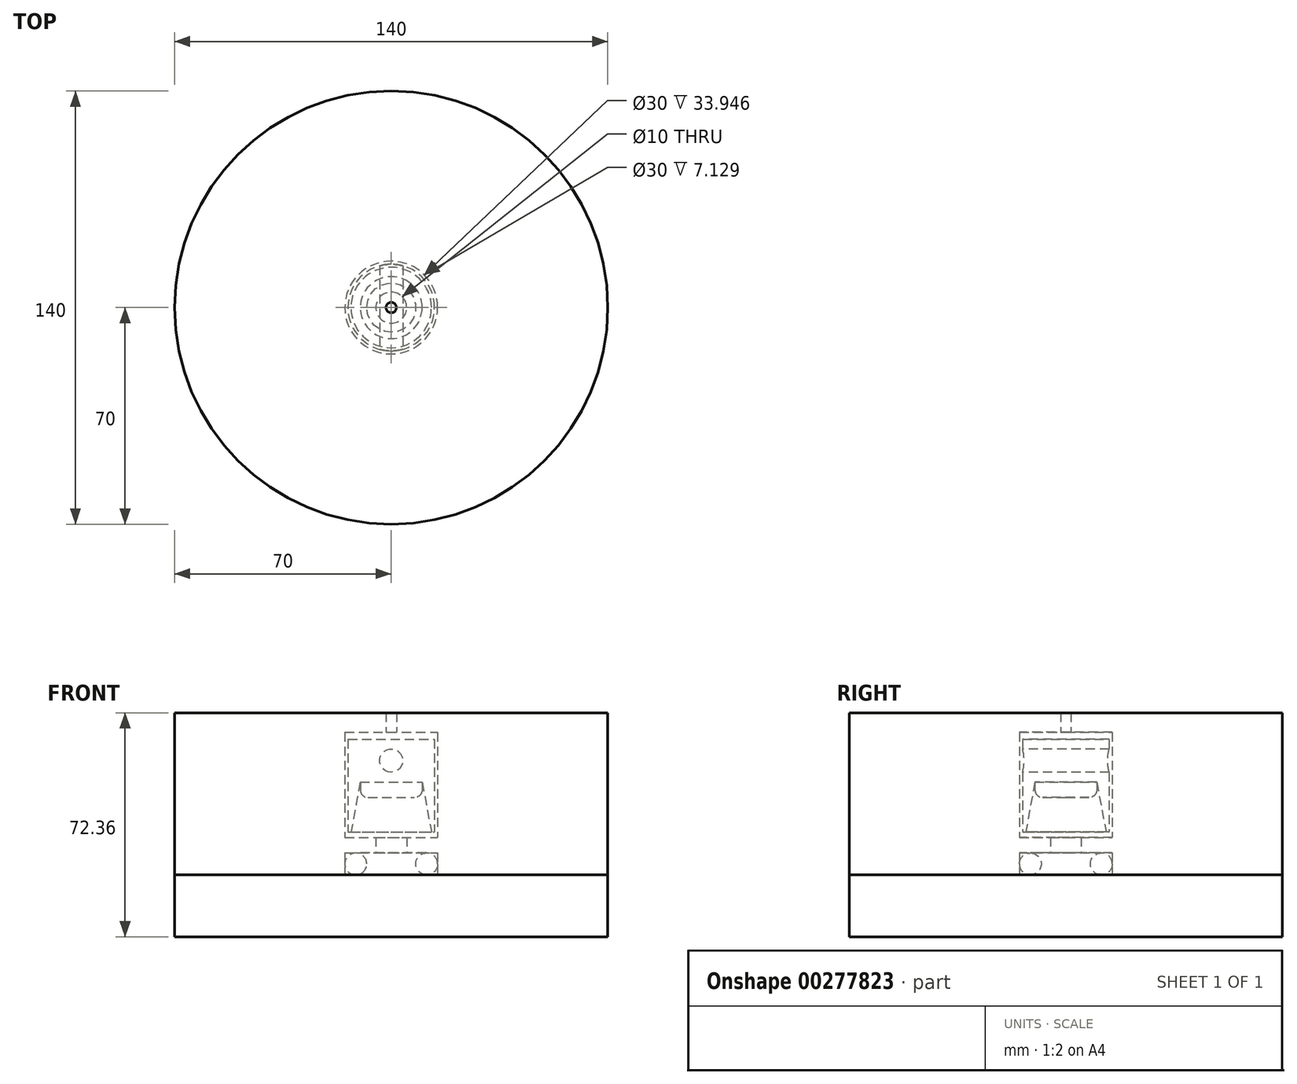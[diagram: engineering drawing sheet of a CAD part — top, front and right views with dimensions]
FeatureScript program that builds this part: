
annotation { "Feature Type Name" : "Feature", "Feature Type Description" : "" }
export const myFeature = defineFeature(function(context is Context, id is Id, definition is map)
    precondition{}
    {
        {
            var Q0;
            Q0=qCreatedBy(makeId("Front.planeOp"),FACE);
            var sketch = newSketch(context, id + "F0", { "sketchPlane" : qUnion([Q0])});
            skLineSegment(sketch, "E0", {"start": v(0, 0) * mm, "end": v(0, 80) * mm, "construction": true});
            skLineSegment(sketch, "E1.bottom", {"start": v(0, 0) * mm, "end": v(15, 0) * mm, "construction": true});
            skLineSegment(sketch, "E1.top", {"start": v(0, 30) * mm, "end": v(15, 30) * mm, "construction": true});
            skLineSegment(sketch, "E1.left", {"start": v(0, 0) * mm, "end": v(0, 30) * mm, "construction": true});
            skLineSegment(sketch, "E1.right", {"start": v(15, 0) * mm, "end": v(15, 30) * mm, "construction": true});
            skLineSegment(sketch, "E2", {"start": v(15, 0) * mm, "end": v(11.46, 3.54) * mm, "construction": true});
            skCircle(sketch, "E3", {"center": v(11.46, 3.54) * mm, "radius": 3.54 * mm});
            skLineSegment(sketch, "E4.bottom", {"start": v(0, 30) * mm, "end": v(10, 30) * mm});
            skLineSegment(sketch, "E4.top", {"start": v(0, 25) * mm, "end": v(7.5, 25) * mm});
            skLineSegment(sketch, "E4.left", {"start": v(0, 30) * mm, "end": v(0, 25) * mm});
            skLineSegment(sketch, "E4.right", {"start": v(10, 30) * mm, "end": v(10, 27.5) * mm});
            skPoint(sketch, "E5.visualSharp", {"position": v(10, 25) * mm});
            skArc(sketch, "E5.filletArc", {"start": v(7.5, 25) * mm, "mid": v(9.27, 25.73) * mm, "end": v(10, 27.5) * mm});
            skLineSegment(sketch, "E6.bottom", {"start": v(0, 30) * mm, "end": v(14, 30) * mm, "construction": true});
            skLineSegment(sketch, "E6.top", {"start": v(0, 13.8) * mm, "end": v(14, 13.8) * mm, "construction": true});
            skLineSegment(sketch, "E6.left", {"start": v(0, 30) * mm, "end": v(0, 13.8) * mm, "construction": true});
            skLineSegment(sketch, "E6.right", {"start": v(14, 30) * mm, "end": v(14, 13.8) * mm, "construction": true});
            skLineSegment(sketch, "E7.bottom", {"start": v(15, 7.13) * mm, "end": v(5, 7.13) * mm});
            skLineSegment(sketch, "E7.top", {"start": v(15, 12.13) * mm, "end": v(5, 12.13) * mm});
            skLineSegment(sketch, "E7.left", {"start": v(15, 7.13) * mm, "end": v(15, 12.13) * mm});
            skLineSegment(sketch, "E7.right", {"start": v(5, 7.13) * mm, "end": v(5, 12.13) * mm});
            skLineSegment(sketch, "E8", {"start": v(10, 30) * mm, "end": v(13, 13.8) * mm});
            skLineSegment(sketch, "E9", {"start": v(13, 13.8) * mm, "end": v(14, 13.8) * mm});
            skLineSegment(sketch, "E10", {"start": v(14, 13.8) * mm, "end": v(14, 43.84) * mm});
            skLineSegment(sketch, "E11", {"start": v(14, 43.84) * mm, "end": v(0, 43.84) * mm});
            skLineSegment(sketch, "E12", {"start": v(0, 43.84) * mm, "end": v(0, 30) * mm});
            skCircle(sketch, "E13", {"center": v(0, 36.92) * mm, "radius": 3.75 * mm});
            skLineSegment(sketch, "E14.bottom", {"start": v(0, 0) * mm, "end": v(70, 0) * mm});
            skLineSegment(sketch, "E14.top", {"start": v(0, -20) * mm, "end": v(70, -20) * mm});
            skLineSegment(sketch, "E14.left", {"start": v(0, 0) * mm, "end": v(0, -20) * mm});
            skLineSegment(sketch, "E14.right", {"start": v(70, 0) * mm, "end": v(70, -20) * mm});
            skLineSegment(sketch, "E15", {"start": v(15, 12.13) * mm, "end": v(15, 46.08) * mm});
            skLineSegment(sketch, "E16", {"start": v(15, 46.08) * mm, "end": v(1.68, 46.08) * mm});
            skLineSegment(sketch, "E17", {"start": v(1.68, 46.08) * mm, "end": v(1.68, 52.36) * mm});
            skLineSegment(sketch, "E18", {"start": v(1.68, 52.36) * mm, "end": v(70, 52.36) * mm});
            skLineSegment(sketch, "E19", {"start": v(70, 52.36) * mm, "end": v(70, 0) * mm});
            skLineSegment(sketch, "E20", {"start": v(70, 0) * mm, "end": v(15, 0) * mm});
            skLineSegment(sketch, "E21", {"start": v(15, 0) * mm, "end": v(15, 7.13) * mm});
            skSolve(sketch);
        }
        {
            var Q0;
            {var subQ0=sQuery(id+"F0.wireOp",EDGE,"E13");var subQ1=sQuery(id+"F0.wireOp",EDGE,"E12");var subQ2=makeQuery(id+"F0.imprint","INTERSECT",VERTEX,{"disambiguationData":[OD(0.0)],"derivedFrom":[subQ1,subQ0]});Q0=makeQuery(id+"F0.imprint","IMPRINT",FACE,{"disambiguationData":[TD([[makeQuery(id+"F0.imprint","IMPRINT",EDGE,{"disambiguationData":[TD([[subQ2,-1.0]])],"derivedFrom":subQ1}),1.0]])]});}
            var Q1;
            {var subQ1=sQuery(id+"F0.wireOp",EDGE,"E4.bottom");Q1=makeQuery(id+"F0.imprint","IMPRINT",FACE,{"disambiguationData":[TD([[makeQuery(id+"F0.imprint","IMPRINT",EDGE,{"derivedFrom":subQ1}),1.0]])]});}
            var Q2;
            Q2=sQuery(id+"F0.wireOp",EDGE,"E1.left");
            revolve(context, id + "F1", {"entities" : qUnion([Q0, Q1]), "axis" : qUnion([Q2]), "revolveType" : RevolveType.FULL});
        }
        {
            var Q0;
            {var subQ0=sQuery(id+"F0.wireOp",EDGE,"E13");var subQ1=sQuery(id+"F0.wireOp",EDGE,"E12");var subQ2=makeQuery(id+"F0.imprint","INTERSECT",VERTEX,{"disambiguationData":[OD(0.0)],"derivedFrom":[subQ1,subQ0]});Q0=makeQuery(id+"F0.imprint","IMPRINT",FACE,{"disambiguationData":[TD([[makeQuery(id+"F0.imprint","IMPRINT",EDGE,{"disambiguationData":[TD([[subQ2,-1.0]])],"derivedFrom":subQ1}),-1.0]])]});}
            var Q1;
            {var subQ0=sQuery(id+"F0.wireOp",EDGE,"E13");var subQ1=sQuery(id+"F0.wireOp",EDGE,"E12");var subQ2=makeQuery(id+"F0.imprint","INTERSECT",VERTEX,{"disambiguationData":[OD(0.0)],"derivedFrom":[subQ1,subQ0]});Q1=makeQuery(id+"F0.imprint","IMPRINT",FACE,{"disambiguationData":[TD([[makeQuery(id+"F0.imprint","IMPRINT",EDGE,{"disambiguationData":[TD([[subQ2,-1.0]])],"derivedFrom":subQ1}),1.0]])]});}
            var Q2;
            Q2=sQuery(id+"F0.wireOp",EDGE,"E13");
            extrude(context, id + "F2", {"entities" : qUnion([Q0, Q1]), "operationType" : NewBodyOperationType.REMOVE, "surfaceEntities" : qUnion([Q2]), "oppositeDirection" : true, "depth" : 28 * mm, "symmetric" : true});
        }
        {
            var Q0;
            Q0=makeQuery(id+"F0.imprint","IMPRINT",FACE,{"disambiguationData":[TD([[makeQuery(id+"F0.imprint","IMPRINT",EDGE,{"derivedFrom":sQuery(id+"F0.wireOp",EDGE,"E3")}),1.0]])]});
            var Q1;
            Q1=sQuery(id+"F0.wireOp",EDGE,"E1.left");
            revolve(context, id + "F3", {"entities" : qUnion([Q0]), "axis" : qUnion([Q1]), "revolveType" : RevolveType.FULL});
        }
        {
            var Q0;
            Q0=makeQuery(id+"F0.imprint","IMPRINT",FACE,{"disambiguationData":[TD([[makeQuery(id+"F0.imprint","IMPRINT",EDGE,{"derivedFrom":sQuery(id+"F0.wireOp",EDGE,"E4.bottom")}),-1.0]])]});
            var Q1;
            Q1=sQuery(id+"F0.wireOp",EDGE,"E1.left");
            revolve(context, id + "F4", {"entities" : qUnion([Q0]), "axis" : qUnion([Q1]), "revolveType" : RevolveType.FULL});
        }
        {
            var Q0;
            {var subQ0=sQuery(id+"F0.wireOp",EDGE,"E7.left");Q0=makeQuery(id+"F0.imprint","IMPRINT",FACE,{"disambiguationData":[TD([[makeQuery(id+"F0.imprint","IMPRINT",EDGE,{"derivedFrom":subQ0}),-1.0]])]});}
            var Q1;
            Q1=makeQuery(id+"F0.imprint","IMPRINT",FACE,{"disambiguationData":[TD([[makeQuery(id+"F0.imprint","IMPRINT",EDGE,{"derivedFrom":sQuery(id+"F0.wireOp",EDGE,"E7.bottom")}),-1.0]])]});
            var Q2;
            Q2=sQuery(id+"F0.wireOp",EDGE,"E1.left");
            revolve(context, id + "F5", {"entities" : qUnion([Q0, Q1]), "axis" : qUnion([Q2]), "revolveType" : RevolveType.FULL});
        }
        {
            var Q0;
            Q0=makeQuery(id+"F0.imprint","IMPRINT",FACE,{"disambiguationData":[TD([[makeQuery(id+"F0.imprint","IMPRINT",EDGE,{"derivedFrom":sQuery(id+"F0.wireOp",EDGE,"E14.top")}),1.0]])]});
            var Q1;
            Q1=sQuery(id+"F0.wireOp",EDGE,"E1.left");
            revolve(context, id + "F6", {"entities" : qUnion([Q0]), "axis" : qUnion([Q1]), "revolveType" : RevolveType.FULL});
        }
    });
